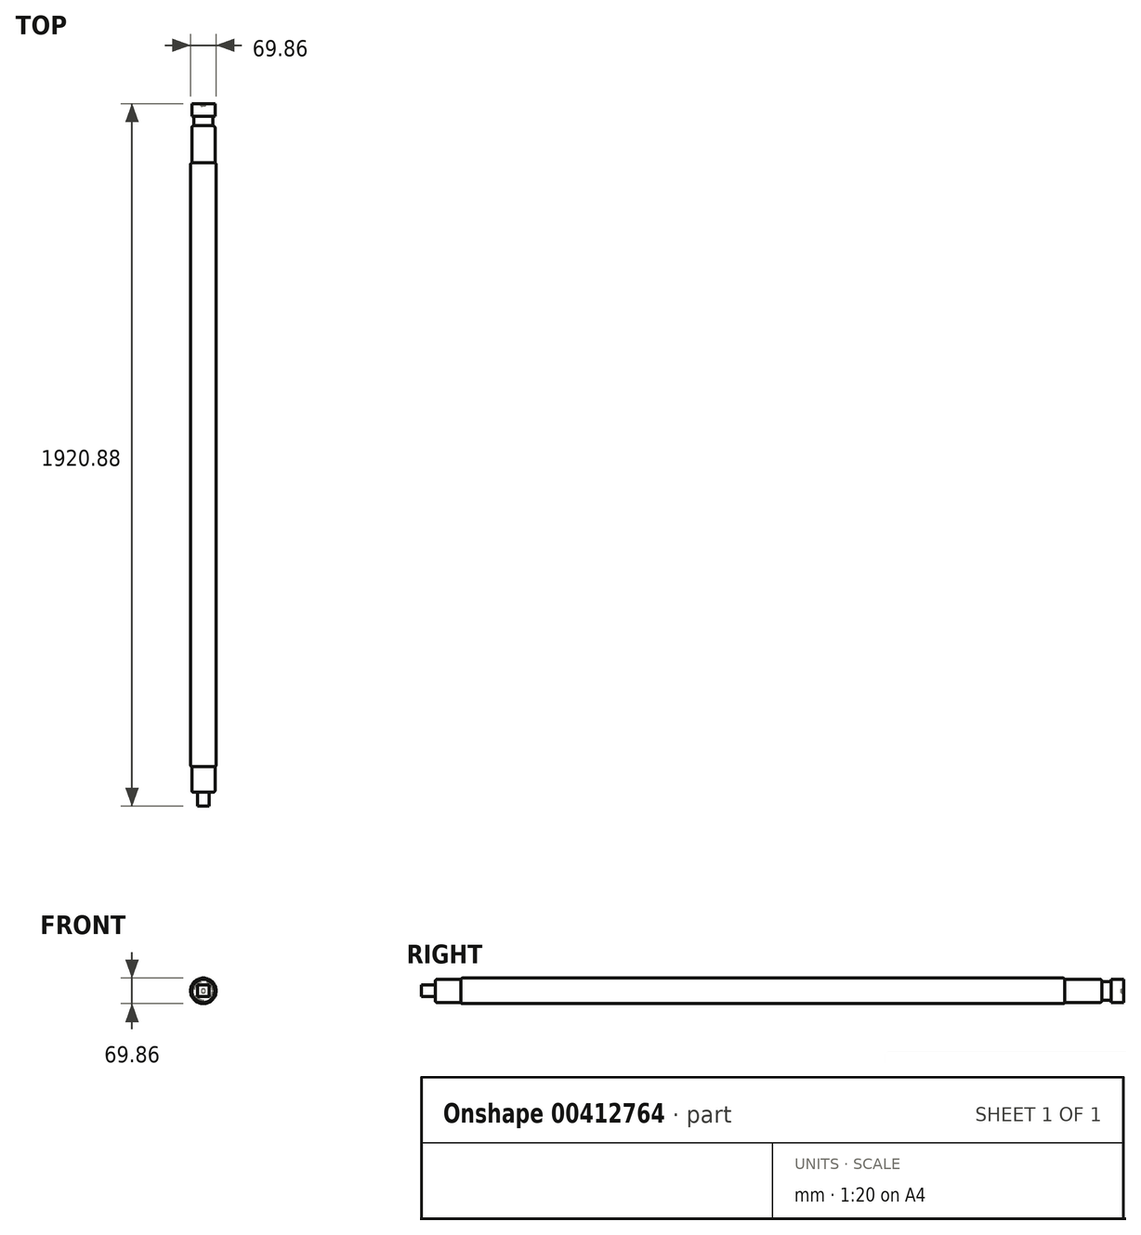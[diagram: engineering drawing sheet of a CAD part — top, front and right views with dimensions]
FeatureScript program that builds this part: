
annotation { "Feature Type Name" : "Feature", "Feature Type Description" : "" }
export const myFeature = defineFeature(function(context is Context, id is Id, definition is map)
    precondition{}
    {
        {
            var Q0;
            Q0=qCreatedBy(makeId("Front.planeOp"),FACE);
            var sketch = newSketch(context, id + "F0", { "sketchPlane" : qUnion([Q0])});
            skCircle(sketch, "E0", {"center": v(0, 0) * mm, "radius": 34.93 * mm});
            skSolve(sketch);
        }
        {
            var Q0;
            Q0 = qSketchRegion(id + "F0", true);
            extrude(context, id + "F1", {"entities" : qUnion([Q0]), "endBound" : BoundingType.SYMMETRIC, "depth" : 1651 * mm, "offsetDistance" : 25.4 * mm});
        }
        {
            var Q0;
            Q0=makeQuery(id+"F1.opExtrude","CAP_FACE",FACE,{"disambiguationData":[OSD([sQuery(id+"F0.wireOp",EDGE,"E0")])],"isStart":false});
            var sketch = newSketch(context, id + "F2", { "sketchPlane" : qUnion([Q0])});
            skCircle(sketch, "E1", {"center": v(0, 0) * mm, "radius": 31.75 * mm});
            skSolve(sketch);
        }
        {
            var Q0;
            Q0 = qSketchRegion(id + "F2", true);
            extrude(context, id + "F3", {"entities" : qUnion([Q0]), "operationType" : NewBodyOperationType.ADD, "depth" : 69.85 * mm, "offsetDistance" : 25.4 * mm});
        }
        {
            var Q0;
            Q0=makeQuery(id+"F1.opExtrude","CAP_FACE",FACE,{"disambiguationData":[OSD([sQuery(id+"F0.wireOp",EDGE,"E0")])],"isStart":true});
            var sketch = newSketch(context, id + "F4", { "sketchPlane" : qUnion([Q0])});
            skCircle(sketch, "E2", {"center": v(0, 0) * mm, "radius": 31.75 * mm});
            skSolve(sketch);
        }
        {
            var Q0;
            Q0 = qSketchRegion(id + "F4", true);
            extrude(context, id + "F5", {"entities" : qUnion([Q0]), "operationType" : NewBodyOperationType.ADD, "depth" : 101.6 * mm, "offsetDistance" : 25.4 * mm});
        }
        {
            var Q0;
            Q0=makeQuery(id+"F3.opExtrude","CAP_FACE",FACE,{"disambiguationData":[OSD([sQuery(id+"F2.wireOp",EDGE,"E1")])],"isStart":false});
            var sketch = newSketch(context, id + "F6", { "sketchPlane" : qUnion([Q0])});
            skLineSegment(sketch, "E3.bottom", {"start": v(15.88, 15.88) * mm, "end": v(-15.88, 15.88) * mm});
            skLineSegment(sketch, "E3.top", {"start": v(15.88, -15.88) * mm, "end": v(-15.88, -15.88) * mm});
            skLineSegment(sketch, "E3.left", {"start": v(15.88, 15.88) * mm, "end": v(15.88, -15.88) * mm});
            skLineSegment(sketch, "E3.right", {"start": v(-15.88, 15.88) * mm, "end": v(-15.88, -15.88) * mm});
            skPoint(sketch, "E3.middle", {"position": v(0, 0) * mm});
            skSolve(sketch);
        }
        {
            var Q0;
            Q0 = qSketchRegion(id + "F6", true);
            extrude(context, id + "F7", {"entities" : qUnion([Q0]), "operationType" : NewBodyOperationType.ADD, "depth" : 38.1 * mm, "offsetDistance" : 25.4 * mm});
        }
        {
            var Q0;
            Q0=makeQuery(id+"F5.opExtrude","CAP_FACE",FACE,{"disambiguationData":[OSD([sQuery(id+"F4.wireOp",EDGE,"E2")])],"isStart":false});
            var sketch = newSketch(context, id + "F8", { "sketchPlane" : qUnion([Q0])});
            skCircle(sketch, "E4", {"center": v(0, 0) * mm, "radius": 25.4 * mm});
            skSolve(sketch);
        }
        {
            var Q0;
            Q0=makeQuery(id+"F8.imprint","IMPRINT",FACE,{"disambiguationData":[TD([[makeQuery(id+"F8.imprint","IMPRINT",EDGE,{"derivedFrom":sQuery(id+"F8.wireOp",EDGE,"E4")}),1.0]])]});
            extrude(context, id + "F9", {"entities" : qUnion([Q0]), "operationType" : NewBodyOperationType.ADD, "depth" : 25.4 * mm, "offsetDistance" : 25.4 * mm});
        }
        {
            var Q0;
            Q0=makeQuery(id+"F9.opExtrude","CAP_FACE",FACE,{"disambiguationData":[OSD([sQuery(id+"F8.wireOp",EDGE,"E4")])],"isStart":false});
            var sketch = newSketch(context, id + "F10", { "sketchPlane" : qUnion([Q0])});
            skCircle(sketch, "E5", {"center": v(0, 0) * mm, "radius": 31.75 * mm});
            skSolve(sketch);
        }
        {
            var Q0;
            Q0=makeQuery(id+"F10.imprint","IMPRINT",FACE,{"disambiguationData":[TD([[makeQuery(id+"F10.imprint","IMPRINT",EDGE,{"derivedFrom":makeQuery(id+"F9.opExtrude","CAP_EDGE",EDGE,{"disambiguationData":[OSD([sQuery(id+"F8.wireOp",EDGE,"E4")])],"isStart":false})}),1.0]])]});
            var Q1;
            Q1=makeQuery(id+"F10.imprint","IMPRINT",FACE,{"disambiguationData":[TD([[makeQuery(id+"F10.imprint","IMPRINT",EDGE,{"derivedFrom":sQuery(id+"F10.wireOp",EDGE,"E5")}),1.0]])]});
            extrude(context, id + "F11", {"entities" : qUnion([Q0, Q1]), "operationType" : NewBodyOperationType.ADD, "depth" : 34.92 * mm, "offsetDistance" : 25.4 * mm});
        }
        {
            var Q0;
            Q0=makeQuery(id+"F1.opExtrude","CAP_EDGE",EDGE,{"disambiguationData":[OSD([sQuery(id+"F0.wireOp",EDGE,"E0")])],"isStart":true});
            var Q1;
            Q1=makeQuery(id+"F1.opExtrude","CAP_EDGE",EDGE,{"disambiguationData":[OSD([sQuery(id+"F0.wireOp",EDGE,"E0")])],"isStart":false});
            var Q2;
            Q2=makeQuery(id+"F3.opExtrude","CAP_EDGE",EDGE,{"disambiguationData":[OSD([sQuery(id+"F2.wireOp",EDGE,"E1")])],"isStart":false});
            var Q3;
            Q3=makeQuery(id+"F5.opExtrude","CAP_EDGE",EDGE,{"disambiguationData":[OSD([sQuery(id+"F4.wireOp",EDGE,"E2")])],"isStart":false});
            fillet(context, id + "F12", {"entities" : qUnion([Q0, Q1, Q2, Q3]), "radius" : 5.08 * mm, "tangentPropagation" : true, "allowEdgeOverflow" : false});
        }
        {
            var Q0;
            Q0=makeQuery(id+"F11.opExtrude","CAP_FACE",FACE,{"disambiguationData":[OSD([sQuery(id+"F10.wireOp",EDGE,"E5")])],"isStart":false});
            var sketch = newSketch(context, id + "F13", { "sketchPlane" : qUnion([Q0])});
            skCircle(sketch, "E6.cCircle", {"center": v(0, 0) * mm, "radius": 4.76 * mm, "construction": true});
            skLineSegment(sketch, "E6.0", {"start": v(-2.75, 4.76) * mm, "end": v(2.75, 4.76) * mm});
            skLineSegment(sketch, "E6.1", {"start": v(2.75, 4.76) * mm, "end": v(5.5, 0) * mm});
            skLineSegment(sketch, "E6.2", {"start": v(5.5, 0) * mm, "end": v(2.75, -4.76) * mm});
            skLineSegment(sketch, "E6.3", {"start": v(2.75, -4.76) * mm, "end": v(-2.75, -4.76) * mm});
            skLineSegment(sketch, "E6.4", {"start": v(-2.75, -4.76) * mm, "end": v(-5.5, 0) * mm});
            skLineSegment(sketch, "E6.5", {"start": v(-5.5, 0) * mm, "end": v(-2.75, 4.76) * mm});
            skPoint(sketch, "E6.0.midPoint", {"position": v(0, 4.76) * mm});
            skSolve(sketch);
        }
        {
            var Q0;
            Q0 = qSketchRegion(id + "F13", true);
            extrude(context, id + "F14", {"entities" : qUnion([Q0]), "operationType" : NewBodyOperationType.REMOVE, "oppositeDirection" : true, "depth" : 6.35 * mm, "offsetDistance" : 25.4 * mm});
        }
    });
